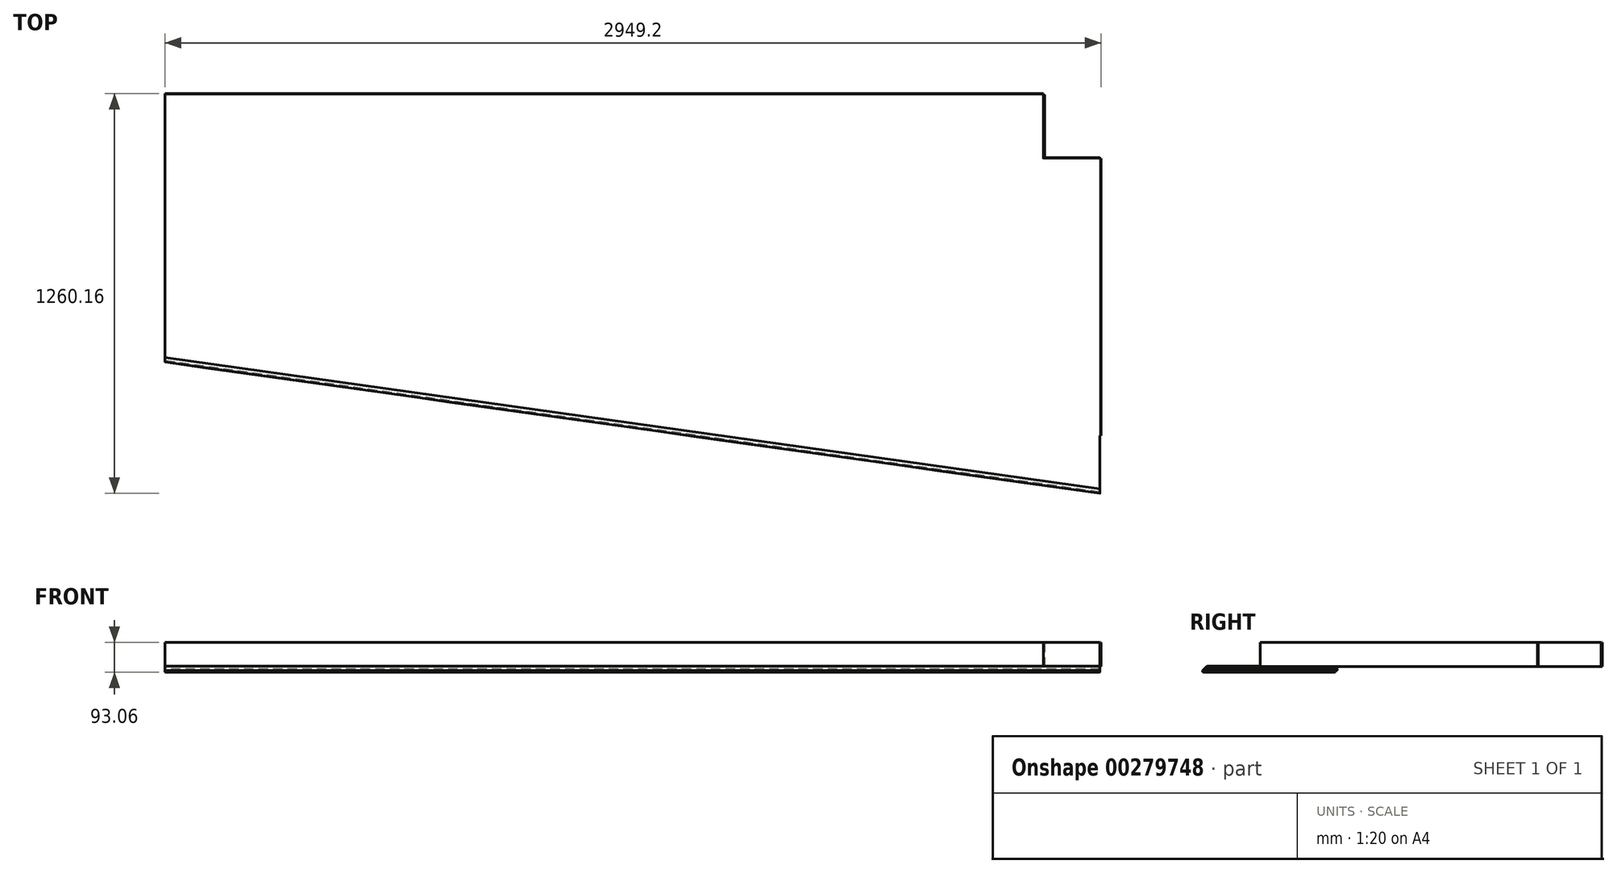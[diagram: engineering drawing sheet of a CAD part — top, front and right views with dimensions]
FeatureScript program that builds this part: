
annotation { "Feature Type Name" : "Feature", "Feature Type Description" : "" }
export const myFeature = defineFeature(function(context is Context, id is Id, definition is map)
    precondition{}
    {
        {
            var Q0;
            Q0=qCreatedBy(makeId("Top.planeOp"),FACE);
            var sketch = newSketch(context, id + "F0", { "sketchPlane" : qUnion([Q0])});
            skLineSegment(sketch, "E0", {"start": v(-1465.82, 723.71) * mm, "end": v(-1465.82, -104.96) * mm});
            skLineSegment(sketch, "E1", {"start": v(-1465.82, -104.96) * mm, "end": v(1480.2, -519) * mm});
            skLineSegment(sketch, "E2", {"start": v(1480.2, -519) * mm, "end": v(1480.2, 522.4) * mm});
            skLineSegment(sketch, "E3", {"start": v(1480.2, 522.4) * mm, "end": v(1302.78, 522.4) * mm});
            skLineSegment(sketch, "E4", {"start": v(1302.78, 522.4) * mm, "end": v(1302.78, 723.71) * mm});
            skLineSegment(sketch, "E5", {"start": v(1302.78, 723.71) * mm, "end": v(-1465.82, 723.71) * mm});
            skSolve(sketch);
        }
        {
            var Q0;
            Q0=makeQuery(id+"F0.imprint","IMPRINT",FACE,{"disambiguationData":[TD([[makeQuery(id+"F0.imprint","IMPRINT",EDGE,{"derivedFrom":sQuery(id+"F0.wireOp",EDGE,"E0")}),1.0]])]});
            extrude(context, id + "F1", {"entities" : qUnion([Q0]), "depth" : 1.31 * mm});
        }
        {
            var Q0;
            Q0=makeQuery(id+"F1.opExtrude","SWEPT_FACE",FACE,{"disambiguationData":[OSD([sQuery(id+"F0.wireOp",EDGE,"E2")])]});
            var sketch = newSketch(context, id + "F2", { "sketchPlane" : qUnion([Q0])});
            skLineSegment(sketch, "E6", {"start": v(-519, 1.31) * mm, "end": v(-532.47, -12.16) * mm});
            skLineSegment(sketch, "E7.0", {"start": v(-519, 0) * mm, "end": v(-531.81, -12.82) * mm});
            skLineSegment(sketch, "E8", {"start": v(-519, 1.31) * mm, "end": v(-519, 0) * mm});
            skArc(sketch, "E9", {"start": v(-532.47, -12.16) * mm, "mid": v(-532.47, -16.05) * mm, "end": v(-528.58, -16.05) * mm});
            skArc(sketch, "E10", {"start": v(-531.81, -12.82) * mm, "mid": v(-531.81, -15.4) * mm, "end": v(-529.23, -15.4) * mm});
            skLineSegment(sketch, "E11", {"start": v(-529.23, -15.4) * mm, "end": v(-520.36, -6.52) * mm});
            skLineSegment(sketch, "E12", {"start": v(-520.36, -6.52) * mm, "end": v(-519.7, -7.18) * mm});
            skLineSegment(sketch, "E13", {"start": v(-519.7, -7.18) * mm, "end": v(-528.58, -16.05) * mm});
            skSolve(sketch);
        }
        {
            var Q0;
            Q0=makeQuery(id+"F2.imprint","IMPRINT",FACE,{"disambiguationData":[TD([[makeQuery(id+"F2.imprint","IMPRINT",EDGE,{"derivedFrom":sQuery(id+"F2.wireOp",EDGE,"E6")}),1.0]])]});
            var Q1;
            Q1=makeQuery(id+"F1.opExtrude","CAP_EDGE",EDGE,{"disambiguationData":[OSD([sQuery(id+"F0.wireOp",EDGE,"E1")])],"isStart":false});
            sweep(context, id + "F3", {"operationType" : NewBodyOperationType.ADD, "profiles" : qUnion([Q0]), "path" : qUnion([Q1]), "keepProfileOrientation" : true});
        }
        {
            var Q0;
            {var subQ0=sQuery(id+"F0.wireOp",EDGE,"E2");Q0=makeQuery(id+"F3.boolean.opBoolean","MERGE",FACE,{"derivedFrom":[makeQuery(id+"F1.opExtrude","SWEPT_FACE",FACE,{"disambiguationData":[OSD([subQ0])]}),makeQuery(id+"F3.opSweep","CAP_FACE",FACE,{"disambiguationData":[OSD([sQuery(id+"F0.wireOp",EDGE,"E1"),subQ0,sQuery(id+"F2.wireOp",EDGE,"E6"),sQuery(id+"F2.wireOp",EDGE,"8NO8RoDA-4JTo-zWKz-X26p-LuDLx8Oe5VgM"),sQuery(id+"F2.wireOp",EDGE,"vrk495PE-NCHl-9HYc-J4hW-jc3xVrfk94fa"),sQuery(id+"F2.wireOp",EDGE,"E7.0"),sQuery(id+"F2.wireOp",EDGE,"8e9dc36c-b58a-4f20-b1f2-07cd3bb17157.0"),sQuery(id+"F2.wireOp",EDGE,"qQYRnucK-Wbkp-6V6j-WAA9-meXws4relTC0"),sQuery(id+"F2.wireOp",EDGE,"A76KDTpO-Wriz-ue8w-teW8-gTTe6CM5fQWZ"),sQuery(id+"F2.wireOp",EDGE,"E8")])],"isStart":true})]});}
            var sketch = newSketch(context, id + "F4", { "sketchPlane" : qUnion([Q0])});
            skLineSegment(sketch, "E14", {"start": v(522.4, 0) * mm, "end": v(522.4, 0) * mm});
            skLineSegment(sketch, "E15", {"start": v(525.58, 3.17) * mm, "end": v(525.58, 76.2) * mm});
            skLineSegment(sketch, "E16", {"start": v(525.58, 76.2) * mm, "end": v(524.27, 76.2) * mm});
            skLineSegment(sketch, "E17", {"start": v(524.27, 76.2) * mm, "end": v(524.27, 4.49) * mm});
            skLineSegment(sketch, "E18", {"start": v(522.4, 1.31) * mm, "end": v(521.1, 1.31) * mm});
            skPoint(sketch, "E19.visualSharp", {"position": v(525.58, 0) * mm});
            skArc(sketch, "E19.filletArc", {"start": v(522.4, 0) * mm, "mid": v(524.65, 0.93) * mm, "end": v(525.58, 3.18) * mm});
            skPoint(sketch, "E20.visualSharp", {"position": v(524.27, 1.31) * mm});
            skArc(sketch, "E20.filletArc", {"start": v(521.1, 1.31) * mm, "mid": v(523.34, 2.24) * mm, "end": v(524.27, 4.49) * mm});
            skSolve(sketch);
        }
        {
            var Q0;
            Q0=makeQuery(id+"F1.opExtrude","SWEPT_FACE",FACE,{"disambiguationData":[OSD([sQuery(id+"F0.wireOp",EDGE,"E3")])]});
            var sketch = newSketch(context, id + "F5", { "sketchPlane" : qUnion([Q0])});
            skLineSegment(sketch, "E21", {"start": v(-1480.2, 0) * mm, "end": v(-1480.2, 0) * mm});
            skLineSegment(sketch, "E22", {"start": v(-1483.38, 3.18) * mm, "end": v(-1483.38, 76.2) * mm});
            skPoint(sketch, "E23.visualSharp", {"position": v(-1483.38, 0) * mm});
            skArc(sketch, "E23.filletArc", {"start": v(-1483.38, 3.18) * mm, "mid": v(-1482.45, 0.93) * mm, "end": v(-1480.2, 0) * mm});
            skLineSegment(sketch, "E24", {"start": v(-1483.38, 76.2) * mm, "end": v(-1482.07, 76.2) * mm});
            skLineSegment(sketch, "E25", {"start": v(-1482.07, 76.2) * mm, "end": v(-1482.07, 4.49) * mm});
            skLineSegment(sketch, "E26", {"start": v(-1478.9, 1.31) * mm, "end": v(-1480.2, 1.31) * mm});
            skPoint(sketch, "E27.visualSharp", {"position": v(-1482.07, 1.31) * mm});
            skArc(sketch, "E27.filletArc", {"start": v(-1482.07, 4.49) * mm, "mid": v(-1481.14, 2.24) * mm, "end": v(-1478.9, 1.31) * mm});
            skSolve(sketch);
        }
        {
            var Q0;
            Q0=makeQuery(id+"F5.imprint","IMPRINT",FACE,{"disambiguationData":[TD([[makeQuery(id+"F5.imprint","IMPRINT",EDGE,{"derivedFrom":sQuery(id+"F5.wireOp",EDGE,"E22")}),-1.0]])]});
            var Q1;
            {var subQ0=sQuery(id+"F0.wireOp",EDGE,"E2");var subQ1=sQuery(id+"F0.wireOp",EDGE,"E1");Q1=makeQuery(id+"F3.boolean.opBoolean","MERGE",VERTEX,{"derivedFrom":[makeQuery(id+"F1.opExtrude","CAP_VERTEX",VERTEX,{"disambiguationData":[OSD([subQ1,subQ0])],"isStart":false}),makeQuery(id+"F3.opSweep","CAP_VERTEX",VERTEX,{"disambiguationData":[OSD([subQ1,subQ0,sQuery(id+"F2.wireOp",EDGE,"E6"),sQuery(id+"F2.wireOp",EDGE,"E8")])],"isStart":true})]});}
            extrude(context, id + "F6", {"entities" : qUnion([Q0]), "operationType" : NewBodyOperationType.ADD, "oppositeDirection" : true, "endBoundEntityVertex" : qUnion([Q1]), "depth" : 873.12 * mm});
        }
        {
            var Q0;
            Q0=makeQuery(id+"F1.opExtrude","SWEPT_FACE",FACE,{"disambiguationData":[OSD([sQuery(id+"F0.wireOp",EDGE,"E4")])]});
            var sketch = newSketch(context, id + "F7", { "sketchPlane" : qUnion([Q0])});
            skLineSegment(sketch, "E28", {"start": v(723.71, 0) * mm, "end": v(723.71, 0) * mm});
            skLineSegment(sketch, "E29", {"start": v(726.89, 3.18) * mm, "end": v(726.89, 76.2) * mm});
            skLineSegment(sketch, "E30", {"start": v(726.89, 76.2) * mm, "end": v(725.58, 76.2) * mm});
            skLineSegment(sketch, "E31", {"start": v(725.58, 76.2) * mm, "end": v(725.58, 4.49) * mm});
            skLineSegment(sketch, "E32", {"start": v(723.71, 1.31) * mm, "end": v(722.4, 1.31) * mm});
            skPoint(sketch, "E33.visualSharp", {"position": v(726.89, 0) * mm});
            skArc(sketch, "E33.filletArc", {"start": v(723.71, 0) * mm, "mid": v(725.96, 0.93) * mm, "end": v(726.89, 3.18) * mm});
            skPoint(sketch, "E34.visualSharp", {"position": v(725.58, 1.31) * mm});
            skArc(sketch, "E34.filletArc", {"start": v(722.4, 1.31) * mm, "mid": v(724.65, 2.24) * mm, "end": v(725.58, 4.49) * mm});
            skSolve(sketch);
        }
        {
            var Q0;
            Q0=makeQuery(id+"F1.opExtrude","SWEPT_FACE",FACE,{"disambiguationData":[OSD([sQuery(id+"F0.wireOp",EDGE,"E5")])]});
            var sketch = newSketch(context, id + "F8", { "sketchPlane" : qUnion([Q0])});
            skLineSegment(sketch, "E35", {"start": v(-1302.78, 0) * mm, "end": v(-1302.78, 0) * mm});
            skLineSegment(sketch, "E36", {"start": v(-1305.95, 3.18) * mm, "end": v(-1305.95, 76.2) * mm});
            skLineSegment(sketch, "E37", {"start": v(-1305.95, 76.2) * mm, "end": v(-1304.64, 76.2) * mm});
            skLineSegment(sketch, "E38", {"start": v(-1304.64, 76.2) * mm, "end": v(-1304.64, 4.48) * mm});
            skLineSegment(sketch, "E39", {"start": v(-1302.78, 1.31) * mm, "end": v(-1301.48, 1.3) * mm});
            skPoint(sketch, "E40.visualSharp", {"position": v(-1305.95, 0) * mm});
            skArc(sketch, "E40.filletArc", {"start": v(-1305.95, 3.17) * mm, "mid": v(-1305.02, 0.93) * mm, "end": v(-1302.78, 0) * mm});
            skPoint(sketch, "E41.visualSharp", {"position": v(-1304.64, 1.32) * mm});
            skArc(sketch, "E41.filletArc", {"start": v(-1304.64, 4.48) * mm, "mid": v(-1303.72, 2.24) * mm, "end": v(-1301.48, 1.3) * mm});
            skSolve(sketch);
        }
        {
            var Q0;
            Q0=makeQuery(id+"F7.imprint","IMPRINT",FACE,{"disambiguationData":[TD([[makeQuery(id+"F7.imprint","IMPRINT",EDGE,{"derivedFrom":sQuery(id+"F7.wireOp",EDGE,"E29")}),1.0]])]});
            var Q1;
            Q1=makeQuery(id+"F1.opExtrude","CAP_VERTEX",VERTEX,{"disambiguationData":[OSD([sQuery(id+"F0.wireOp",EDGE,"E0"),sQuery(id+"F0.wireOp",EDGE,"E5")])],"isStart":false});
            extrude(context, id + "F9", {"entities" : qUnion([Q0]), "operationType" : NewBodyOperationType.ADD, "endBound" : BoundingType.UP_TO_VERTEX, "oppositeDirection" : true, "endBoundEntityVertex" : qUnion([Q1]), "depth" : 25.4 * mm});
        }
        {
            var Q0;
            Q0=makeQuery(id+"F4.imprint","IMPRINT",FACE,{"disambiguationData":[TD([[makeQuery(id+"F4.imprint","IMPRINT",EDGE,{"derivedFrom":sQuery(id+"F4.wireOp",EDGE,"E15")}),1.0]])]});
            var Q1;
            {var subQ0=sQuery(id+"F0.wireOp",EDGE,"E4");Q1=makeQuery(id+"F9.boolean.opBoolean","MERGE",FACE,{"derivedFrom":[makeQuery(id+"F1.opExtrude","SWEPT_FACE",FACE,{"disambiguationData":[OSD([subQ0])]}),makeQuery(id+"F9.opExtrude","CAP_FACE",FACE,{"disambiguationData":[OSD([subQ0,sQuery(id+"F0.wireOp",EDGE,"E5"),sQuery(id+"F7.wireOp",EDGE,"E29"),sQuery(id+"F7.wireOp",EDGE,"E30"),sQuery(id+"F7.wireOp",EDGE,"E31"),sQuery(id+"F7.wireOp",EDGE,"E32"),sQuery(id+"F7.wireOp",EDGE,"E33.filletArc"),sQuery(id+"F7.wireOp",EDGE,"E34.filletArc")])],"isStart":true})]});}
            extrude(context, id + "F10", {"entities" : qUnion([Q0]), "operationType" : NewBodyOperationType.ADD, "endBound" : BoundingType.UP_TO_SURFACE, "oppositeDirection" : true, "endBoundEntityFace" : qUnion([Q1]), "depth" : 25.4 * mm});
        }
        {
            var Q0;
            Q0=makeQuery(id+"F8.imprint","IMPRINT",FACE,{"disambiguationData":[TD([[makeQuery(id+"F8.imprint","IMPRINT",EDGE,{"derivedFrom":sQuery(id+"F8.wireOp",EDGE,"E36")}),-1.0]])]});
            var Q1;
            Q1=makeQuery(id+"F10.opExtrude","SWEPT_FACE",FACE,{"disambiguationData":[OSD([sQuery(id+"F4.wireOp",EDGE,"E15")])]});
            extrude(context, id + "F11", {"entities" : qUnion([Q0]), "operationType" : NewBodyOperationType.ADD, "endBound" : BoundingType.UP_TO_SURFACE, "oppositeDirection" : true, "endBoundEntityFace" : qUnion([Q1]), "depth" : 25.4 * mm});
        }
    });
